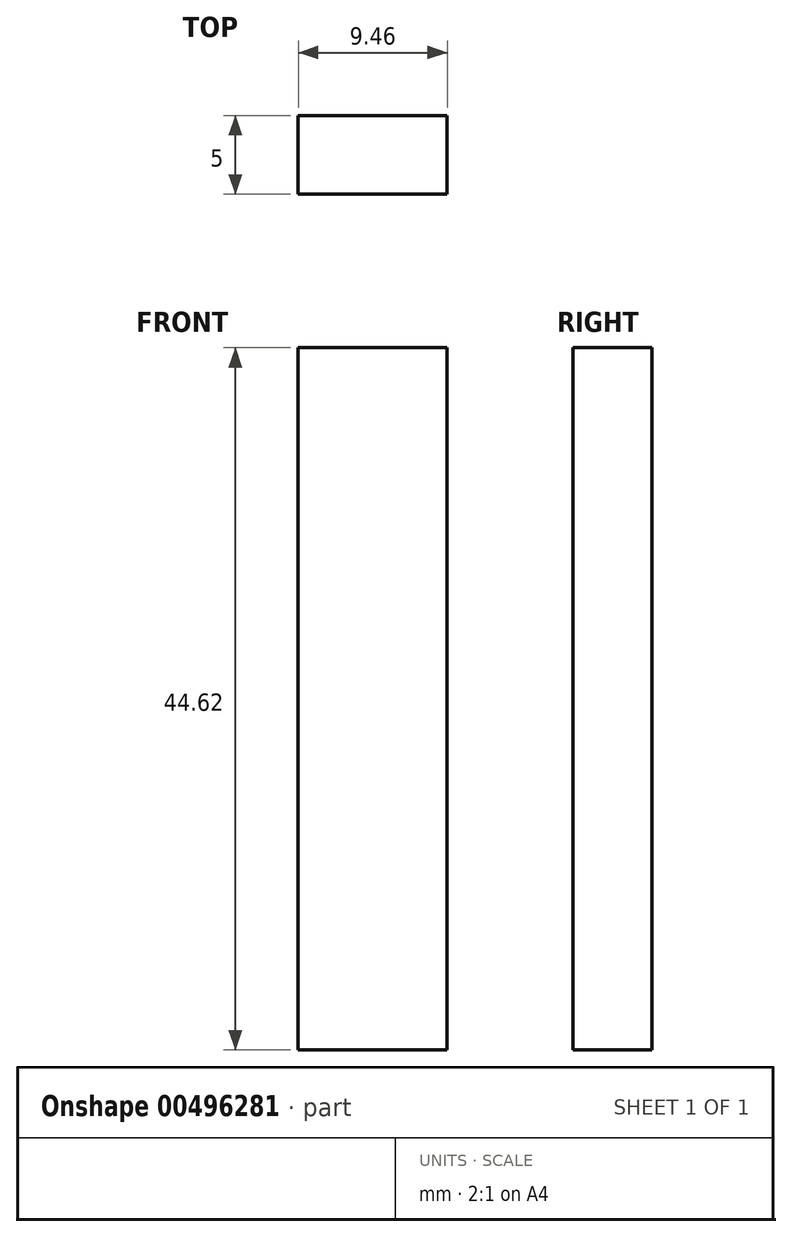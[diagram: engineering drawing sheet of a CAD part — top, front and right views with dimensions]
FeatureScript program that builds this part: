
annotation { "Feature Type Name" : "Feature", "Feature Type Description" : "" }
export const myFeature = defineFeature(function(context is Context, id is Id, definition is map)
    precondition{}
    {
        {
            var Q0;
            Q0=qCreatedBy(makeId("Front.planeOp"),FACE);
            var sketch = newSketch(context, id + "F0", { "sketchPlane" : qUnion([Q0])});
            skText(sketch, "E0", { "text": "I", "fontName": "OpenSans-Bold.ttf"});
            const initialGuessF0  = {"E0": [-0.04912, 0.0058, 1, 0, 0.045]};
            skSetInitialGuess(sketch, initialGuessF0);
            skSolve(sketch);
        }
        {
            var Q0;
            Q0=makeQuery(id+"F0.imprint","IMPRINT",FACE,{"disambiguationData":[TD([[makeQuery(id+"F0.imprint","IMPRINT",EDGE,{"derivedFrom":sQuery(id+"F0.wireOp",EDGE,"E0.sketch_text.stroke-0")}),-1.0]])]});
            extrude(context, id + "F1", {"entities" : qUnion([Q0]), "depth" : 5 * mm});
        }
    });
